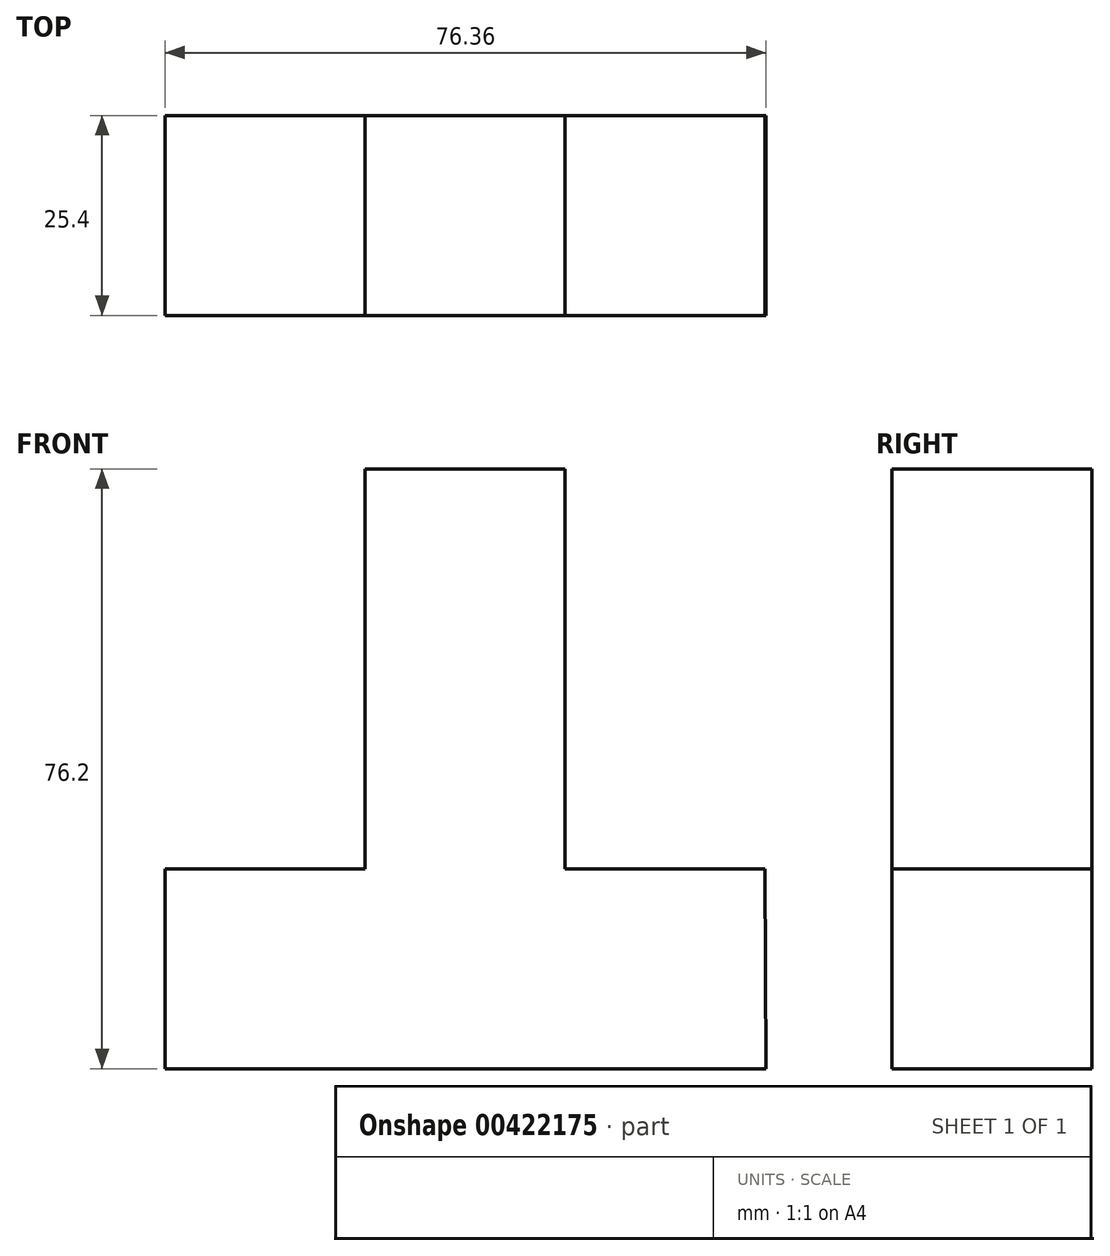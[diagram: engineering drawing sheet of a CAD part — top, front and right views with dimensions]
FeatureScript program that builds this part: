
annotation { "Feature Type Name" : "Feature", "Feature Type Description" : "" }
export const myFeature = defineFeature(function(context is Context, id is Id, definition is map)
    precondition{}
    {
        {
            var Q0;
            Q0=qCreatedBy(makeId("Front.planeOp"),FACE);
            var sketch = newSketch(context, id + "F0", { "sketchPlane" : qUnion([Q0])});
            skLineSegment(sketch, "E0", {"start": v(-61.27, -25.4) * mm, "end": v(15.1, -25.4) * mm});
            skLineSegment(sketch, "E1", {"start": v(-61.27, -25.4) * mm, "end": v(-61.27, 0) * mm});
            skLineSegment(sketch, "E2", {"start": v(-61.27, 0) * mm, "end": v(-35.87, 0) * mm});
            skLineSegment(sketch, "E3", {"start": v(-35.87, 0) * mm, "end": v(-35.87, 50.8) * mm});
            skLineSegment(sketch, "E4", {"start": v(-35.87, 50.8) * mm, "end": v(-10.47, 50.8) * mm});
            skLineSegment(sketch, "E5", {"start": v(-10.47, 50.8) * mm, "end": v(-10.47, 0) * mm});
            skLineSegment(sketch, "E6", {"start": v(-10.47, 0) * mm, "end": v(14.93, 0) * mm});
            skLineSegment(sketch, "E7", {"start": v(14.93, 0) * mm, "end": v(15.1, -25.4) * mm});
            skSolve(sketch);
        }
        {
            var Q0;
            Q0 = qSketchRegion(id + "F0", true);
            extrude(context, id + "F1", {"entities" : qUnion([Q0]), "depth" : 25.4 * mm});
        }
    });
